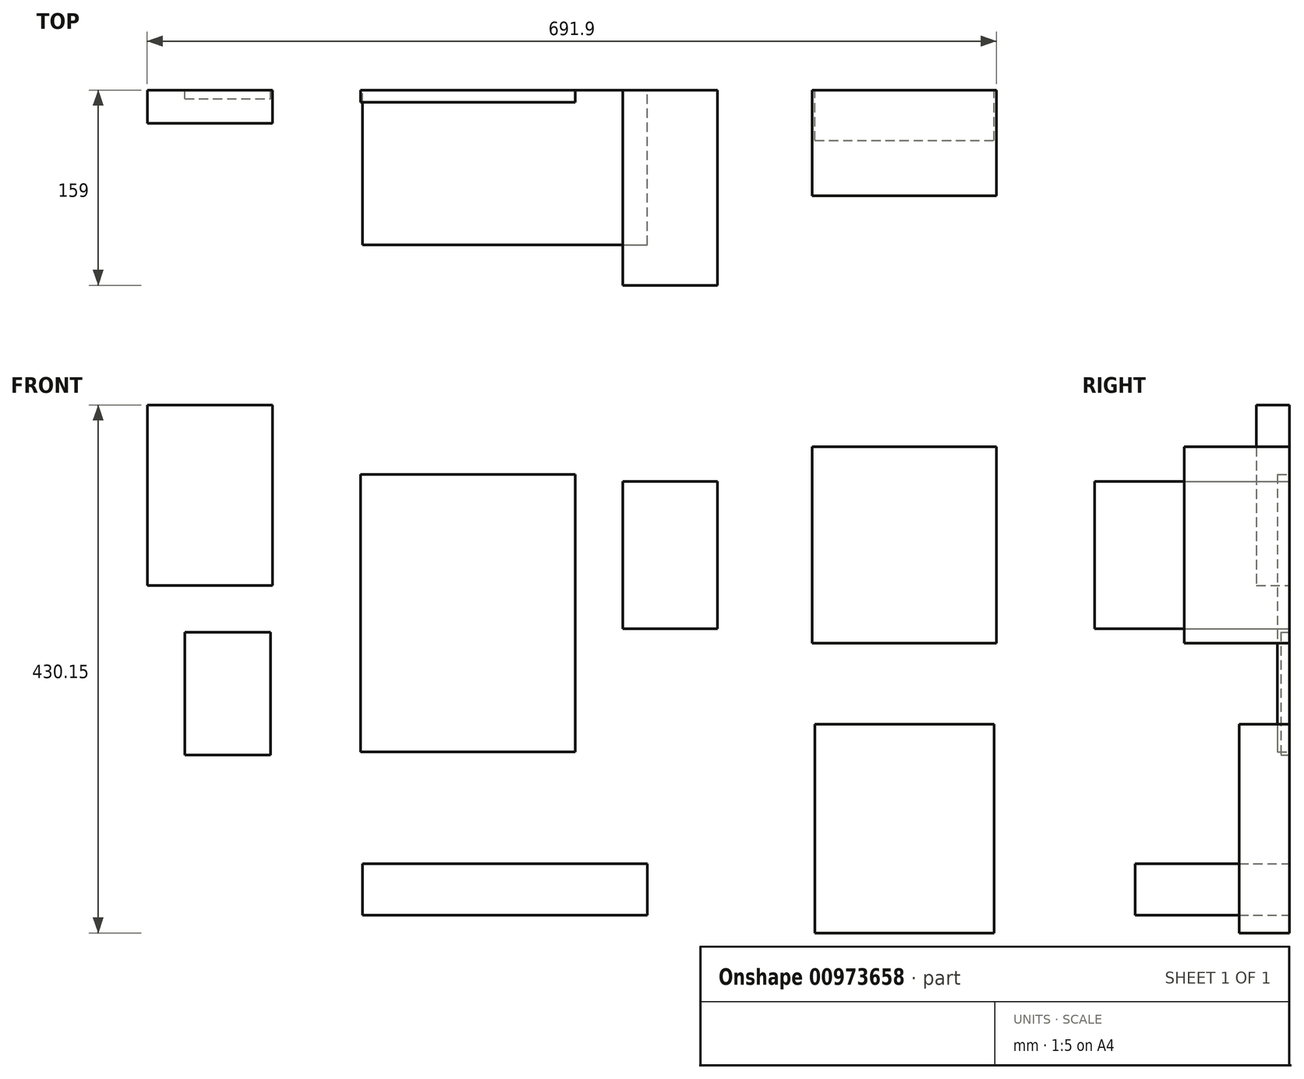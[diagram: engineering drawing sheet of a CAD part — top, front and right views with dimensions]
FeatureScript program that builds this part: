
annotation { "Feature Type Name" : "Feature", "Feature Type Description" : "" }
export const myFeature = defineFeature(function(context is Context, id is Id, definition is map)
    precondition{}
    {
        {
            var Q0;
            Q0=qCreatedBy(makeId("Front.planeOp"),FACE);
            var sketch = newSketch(context, id + "F0", { "sketchPlane" : qUnion([Q0])});
            skLineSegment(sketch, "E0.bottom", {"start": v(-174.57, 106.8) * mm, "end": v(0.43, 106.8) * mm});
            skLineSegment(sketch, "E0.top", {"start": v(-174.57, -119.2) * mm, "end": v(0.43, -119.2) * mm});
            skLineSegment(sketch, "E0.left", {"start": v(-174.57, 106.8) * mm, "end": v(-174.57, -119.2) * mm});
            skLineSegment(sketch, "E0.right", {"start": v(0.43, 106.8) * mm, "end": v(0.43, -119.2) * mm});
            skLineSegment(sketch, "E1.bottom", {"start": v(39.14, 101.05) * mm, "end": v(116.14, 101.05) * mm});
            skLineSegment(sketch, "E1.top", {"start": v(39.14, -18.95) * mm, "end": v(116.14, -18.95) * mm});
            skLineSegment(sketch, "E1.left", {"start": v(39.14, 101.05) * mm, "end": v(39.14, -18.95) * mm});
            skLineSegment(sketch, "E1.right", {"start": v(116.14, 101.05) * mm, "end": v(116.14, -18.95) * mm});
            skLineSegment(sketch, "E2.bottom", {"start": v(193.42, 129.46) * mm, "end": v(343.42, 129.46) * mm});
            skLineSegment(sketch, "E2.top", {"start": v(193.42, -30.54) * mm, "end": v(343.42, -30.54) * mm});
            skLineSegment(sketch, "E2.left", {"start": v(193.42, 129.46) * mm, "end": v(193.42, -30.54) * mm});
            skLineSegment(sketch, "E2.right", {"start": v(343.42, 129.46) * mm, "end": v(343.42, -30.54) * mm});
            skLineSegment(sketch, "E3.bottom", {"start": v(195.6, -96.68) * mm, "end": v(341.6, -96.68) * mm});
            skLineSegment(sketch, "E3.top", {"start": v(195.6, -266.68) * mm, "end": v(341.6, -266.68) * mm});
            skLineSegment(sketch, "E3.left", {"start": v(195.6, -96.68) * mm, "end": v(195.6, -266.68) * mm});
            skLineSegment(sketch, "E3.right", {"start": v(341.6, -96.68) * mm, "end": v(341.6, -266.68) * mm});
            skLineSegment(sketch, "E4.bottom", {"start": v(-173.1, -210.2) * mm, "end": v(58.9, -210.2) * mm});
            skLineSegment(sketch, "E4.top", {"start": v(-173.1, -252.2) * mm, "end": v(58.9, -252.2) * mm});
            skLineSegment(sketch, "E4.left", {"start": v(-173.1, -210.2) * mm, "end": v(-173.1, -252.2) * mm});
            skLineSegment(sketch, "E4.right", {"start": v(58.9, -210.2) * mm, "end": v(58.9, -252.2) * mm});
            skLineSegment(sketch, "E5.bottom", {"start": v(-348.48, 163.47) * mm, "end": v(-246.48, 163.47) * mm});
            skLineSegment(sketch, "E5.top", {"start": v(-348.48, 16.47) * mm, "end": v(-246.48, 16.47) * mm});
            skLineSegment(sketch, "E5.left", {"start": v(-348.48, 163.47) * mm, "end": v(-348.48, 16.47) * mm});
            skLineSegment(sketch, "E5.right", {"start": v(-246.48, 163.47) * mm, "end": v(-246.48, 16.47) * mm});
            skLineSegment(sketch, "E6.bottom", {"start": v(-317.86, -21.62) * mm, "end": v(-247.86, -21.62) * mm});
            skLineSegment(sketch, "E6.top", {"start": v(-317.86, -121.62) * mm, "end": v(-247.86, -121.62) * mm});
            skLineSegment(sketch, "E6.left", {"start": v(-317.86, -21.62) * mm, "end": v(-317.86, -121.62) * mm});
            skLineSegment(sketch, "E6.right", {"start": v(-247.86, -21.62) * mm, "end": v(-247.86, -121.62) * mm});
            skSolve(sketch);
        }
        {
            var Q0;
            Q0=makeQuery(id+"F0.imprint","IMPRINT",FACE,{"disambiguationData":[TD([[makeQuery(id+"F0.imprint","IMPRINT",EDGE,{"derivedFrom":sQuery(id+"F0.wireOp",EDGE,"E0.bottom")}),-1.0]])]});
            var Q1;
            Q1=sQuery(id+"F0.wireOp",EDGE,"E0.right");
            var Q2;
            Q2=sQuery(id+"F0.wireOp",EDGE,"E0.bottom");
            var Q3;
            Q3=sQuery(id+"F0.wireOp",EDGE,"E0.left");
            var Q4;
            Q4=sQuery(id+"F0.wireOp",EDGE,"E0.top");
            extrude(context, id + "F1", {"entities" : qUnion([Q0]), "surfaceEntities" : qUnion([Q1, Q2, Q3, Q4]), "depth" : 10 * mm, "offsetDistance" : 25 * mm});
        }
        {
            var Q0;
            Q0=makeQuery(id+"F0.imprint","IMPRINT",FACE,{"disambiguationData":[TD([[makeQuery(id+"F0.imprint","IMPRINT",EDGE,{"derivedFrom":sQuery(id+"F0.wireOp",EDGE,"E1.bottom")}),-1.0]])]});
            var Q1;
            Q1=sQuery(id+"F0.wireOp",EDGE,"E1.top");
            var Q2;
            Q2=sQuery(id+"F0.wireOp",EDGE,"E1.right");
            var Q3;
            Q3=sQuery(id+"F0.wireOp",EDGE,"E1.bottom");
            var Q4;
            Q4=sQuery(id+"F0.wireOp",EDGE,"E1.left");
            extrude(context, id + "F2", {"entities" : qUnion([Q0]), "surfaceEntities" : qUnion([Q1, Q2, Q3, Q4]), "depth" : 159 * mm, "offsetDistance" : 25 * mm});
        }
        {
            var Q0;
            Q0=makeQuery(id+"F0.imprint","IMPRINT",FACE,{"disambiguationData":[TD([[makeQuery(id+"F0.imprint","IMPRINT",EDGE,{"derivedFrom":sQuery(id+"F0.wireOp",EDGE,"E2.bottom")}),-1.0]])]});
            var Q1;
            Q1=sQuery(id+"F0.wireOp",EDGE,"E2.bottom");
            var Q2;
            Q2=sQuery(id+"F0.wireOp",EDGE,"E2.right");
            var Q3;
            Q3=sQuery(id+"F0.wireOp",EDGE,"E2.top");
            var Q4;
            Q4=sQuery(id+"F0.wireOp",EDGE,"E2.left");
            extrude(context, id + "F3", {"entities" : qUnion([Q0]), "surfaceEntities" : qUnion([Q1, Q2, Q3, Q4]), "depth" : 86 * mm, "offsetDistance" : 25 * mm});
        }
        {
            var Q0;
            Q0=makeQuery(id+"F0.imprint","IMPRINT",FACE,{"disambiguationData":[TD([[makeQuery(id+"F0.imprint","IMPRINT",EDGE,{"derivedFrom":sQuery(id+"F0.wireOp",EDGE,"E4.bottom")}),-1.0]])]});
            var Q1;
            Q1=sQuery(id+"F0.wireOp",EDGE,"E2.bottom");
            var Q2;
            Q2=sQuery(id+"F0.wireOp",EDGE,"E2.right");
            var Q3;
            Q3=sQuery(id+"F0.wireOp",EDGE,"E2.top");
            var Q4;
            Q4=sQuery(id+"F0.wireOp",EDGE,"E2.left");
            extrude(context, id + "F4", {"entities" : qUnion([Q0]), "surfaceEntities" : qUnion([Q1, Q2, Q3, Q4]), "depth" : 126 * mm, "offsetDistance" : 25 * mm});
        }
        {
            var Q0;
            Q0=makeQuery(id+"F0.imprint","IMPRINT",FACE,{"disambiguationData":[TD([[makeQuery(id+"F0.imprint","IMPRINT",EDGE,{"derivedFrom":sQuery(id+"F0.wireOp",EDGE,"E3.bottom")}),-1.0]])]});
            extrude(context, id + "F5", {"entities" : qUnion([Q0]), "depth" : 41 * mm, "offsetDistance" : 25 * mm});
        }
        {
            var Q0;
            Q0=makeQuery(id+"F0.imprint","IMPRINT",FACE,{"disambiguationData":[TD([[makeQuery(id+"F0.imprint","IMPRINT",EDGE,{"derivedFrom":sQuery(id+"F0.wireOp",EDGE,"E5.bottom")}),-1.0]])]});
            extrude(context, id + "F6", {"entities" : qUnion([Q0]), "depth" : 27 * mm, "offsetDistance" : 25 * mm});
        }
        {
            var Q0;
            Q0=makeQuery(id+"F0.imprint","IMPRINT",FACE,{"disambiguationData":[TD([[makeQuery(id+"F0.imprint","IMPRINT",EDGE,{"derivedFrom":sQuery(id+"F0.wireOp",EDGE,"E6.bottom")}),-1.0]])]});
            extrude(context, id + "F7", {"entities" : qUnion([Q0]), "depth" : 7 * mm, "offsetDistance" : 25 * mm});
        }
    });
